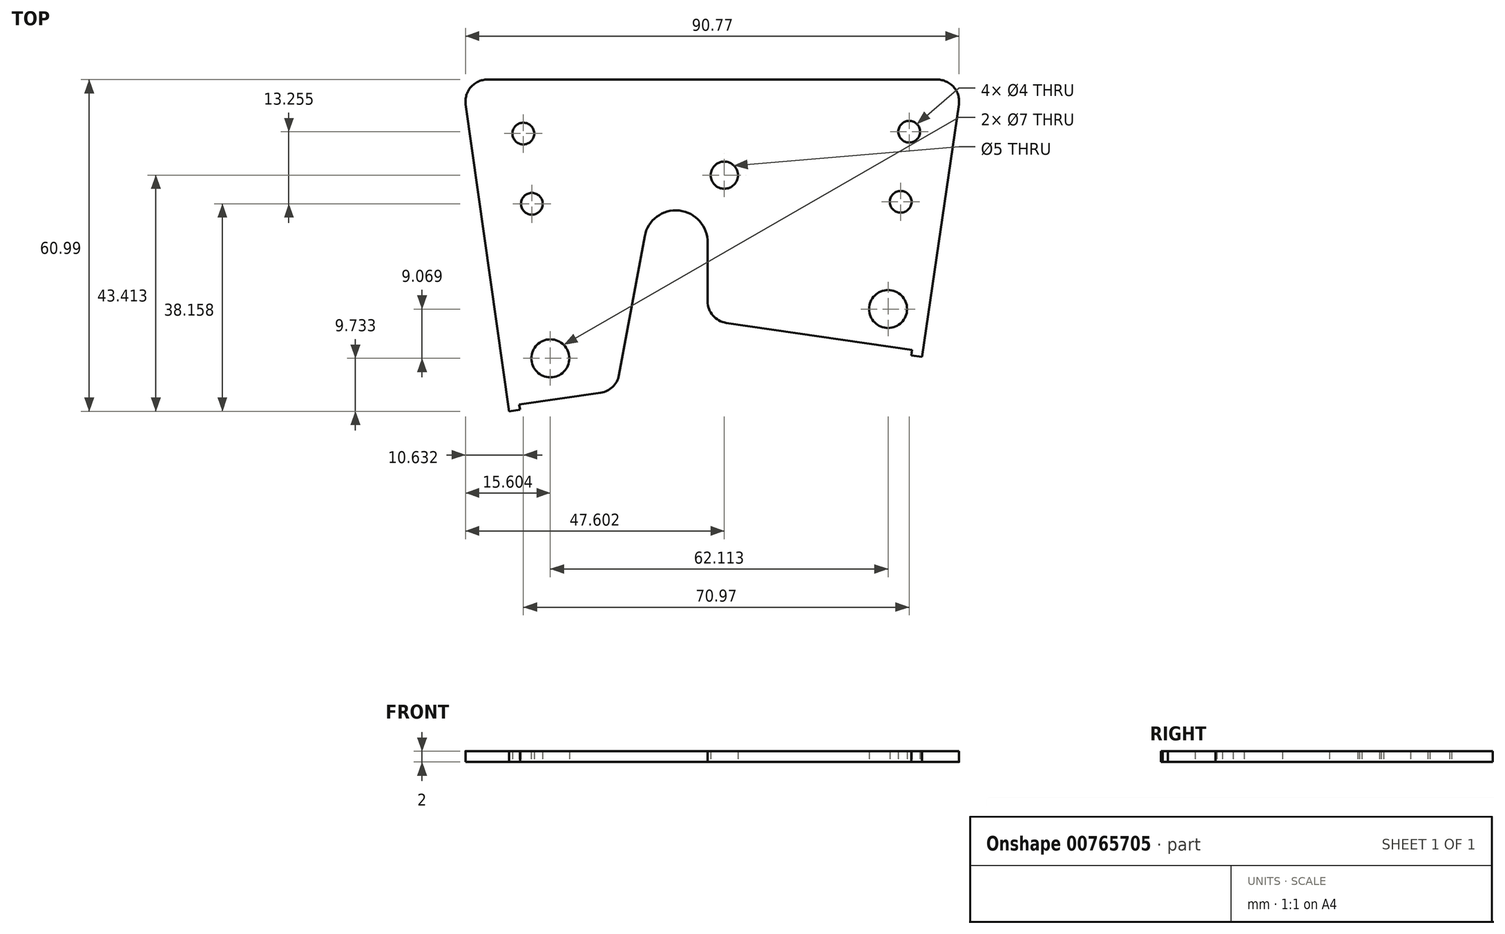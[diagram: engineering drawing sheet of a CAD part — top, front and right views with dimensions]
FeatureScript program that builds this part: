
annotation { "Feature Type Name" : "Feature", "Feature Type Description" : "" }
export const myFeature = defineFeature(function(context is Context, id is Id, definition is map)
    precondition{}
    {
        {
            var Q0;
            Q0=qCreatedBy(makeId("Top.planeOp"),FACE);
            var sketch = newSketch(context, id + "F0", { "sketchPlane" : qUnion([Q0])});
            skLineSegment(sketch, "E0", {"start": v(-34.56, 39.14) * mm, "end": v(48.21, 39.14) * mm});
            skLineSegment(sketch, "E1", {"start": v(-38.52, 34.58) * mm, "end": v(-30.66, -20.86) * mm});
            skLineSegment(sketch, "E2", {"start": v(52.17, 34.57) * mm, "end": v(45.55, -10.86) * mm});
            skLineSegment(sketch, "E3", {"start": v(-28.68, -20.58) * mm, "end": v(-13.71, -18.46) * mm});
            skLineSegment(sketch, "E4", {"start": v(43.57, -10.57) * mm, "end": v(9.4, -5.59) * mm});
            skArc(sketch, "E5", {"start": v(5.97, 9.1) * mm, "mid": v(0.73, 15.06) * mm, "end": v(-5.62, 10.3) * mm});
            skLineSegment(sketch, "E6", {"start": v(-10.34, -15.22) * mm, "end": v(-5.62, 10.3) * mm});
            skLineSegment(sketch, "E7", {"start": v(5.97, -1.63) * mm, "end": v(5.97, 9.1) * mm});
            skPoint(sketch, "E8.visualSharp", {"position": v(-10.86, -18.05) * mm});
            skArc(sketch, "E8.filletArc", {"start": v(-13.71, -18.46) * mm, "mid": v(-11.5, -17.38) * mm, "end": v(-10.34, -15.22) * mm});
            skPoint(sketch, "E9.visualSharp", {"position": v(-39.16, 39.14) * mm});
            skArc(sketch, "E9.filletArc", {"start": v(-34.56, 39.14) * mm, "mid": v(-37.58, 37.76) * mm, "end": v(-38.52, 34.58) * mm});
            skPoint(sketch, "E10.visualSharp", {"position": v(52.84, 39.14) * mm});
            skArc(sketch, "E10.filletArc", {"start": v(52.17, 34.57) * mm, "mid": v(51.24, 37.76) * mm, "end": v(48.21, 39.14) * mm});
            skPoint(sketch, "E11.visualSharp", {"position": v(5.97, -5.1) * mm});
            skArc(sketch, "E11.filletArc", {"start": v(5.97, -1.63) * mm, "mid": v(6.94, -4.25) * mm, "end": v(9.4, -5.59) * mm});
            skPoint(sketch, "E12.endSnap0", {"position": v(-22.19, -19.66) * mm});
            skCircle(sketch, "E13", {"center": v(-27.93, 29.21) * mm, "radius": 2 * mm});
            skCircle(sketch, "E14", {"center": v(-26.36, 16.3) * mm, "radius": 2 * mm});
            skCircle(sketch, "E15", {"center": v(-22.96, -12.12) * mm, "radius": 3.5 * mm});
            skCircle(sketch, "E16", {"center": v(9.04, 21.56) * mm, "radius": 2.5 * mm});
            skCircle(sketch, "E17", {"center": v(43.04, 29.56) * mm, "radius": 2 * mm});
            skCircle(sketch, "E18", {"center": v(41.47, 16.66) * mm, "radius": 2 * mm});
            skCircle(sketch, "E19", {"center": v(39.16, -3.05) * mm, "radius": 3.5 * mm});
            skLineSegment(sketch, "E20", {"start": v(-30.66, -20.86) * mm, "end": v(-30.52, -21.85) * mm});
            skLineSegment(sketch, "E21", {"start": v(-30.52, -21.85) * mm, "end": v(-28.54, -21.57) * mm});
            skLineSegment(sketch, "E22", {"start": v(-28.54, -21.57) * mm, "end": v(-28.68, -20.58) * mm});
            skLineSegment(sketch, "E23", {"start": v(45.55, -10.86) * mm, "end": v(45.4, -11.85) * mm});
            skLineSegment(sketch, "E24", {"start": v(45.4, -11.85) * mm, "end": v(43.43, -11.56) * mm});
            skLineSegment(sketch, "E25", {"start": v(43.43, -11.56) * mm, "end": v(43.57, -10.57) * mm});
            skSolve(sketch);
        }
        {
            var Q0;
            Q0=makeQuery(id+"F0.imprint","IMPRINT",FACE,{"disambiguationData":[TD([[makeQuery(id+"F0.imprint","IMPRINT",EDGE,{"derivedFrom":sQuery(id+"F0.wireOp",EDGE,"E0")}),-1.0]])]});
            extrude(context, id + "F1", {"entities" : qUnion([Q0]), "depth" : 2 * mm, "offsetDistance" : 25 * mm});
        }
    });
